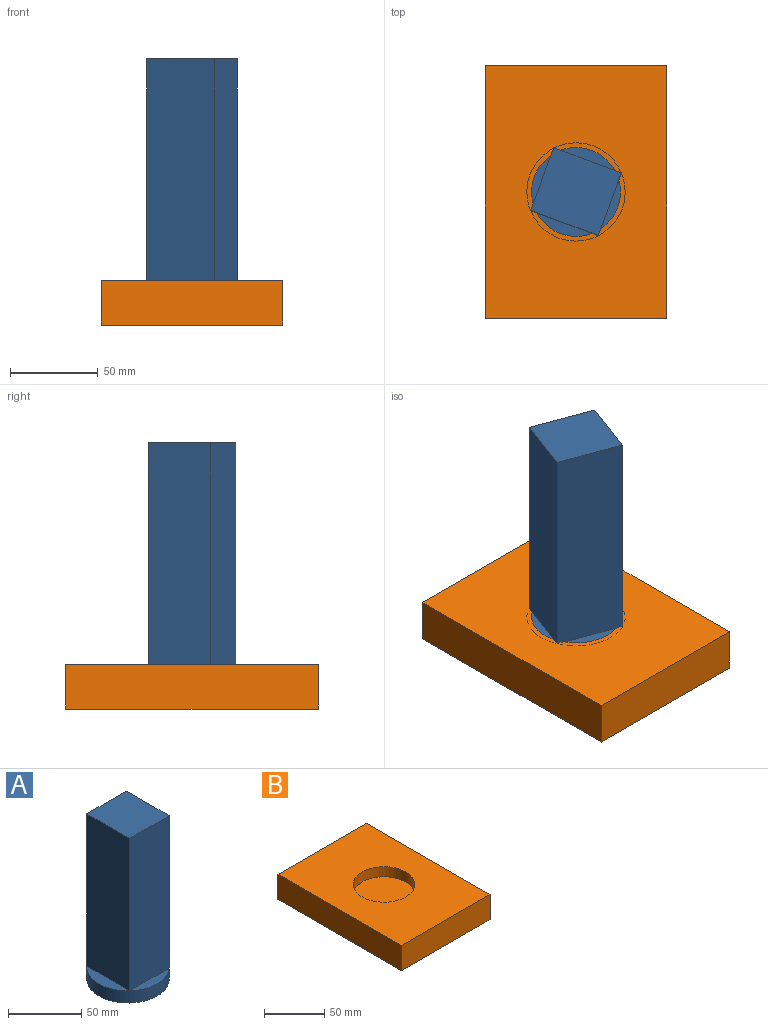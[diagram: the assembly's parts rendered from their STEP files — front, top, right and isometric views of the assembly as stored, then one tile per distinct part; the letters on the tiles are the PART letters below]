
ASSEMBLY  parts=2 mates=1
PART A: 11 faces, bbox 56.2x56.2x137.2 mm
  f0: plane 38.1x7.45mm, normal (0,0,1), area 194.9mm2, adj f3,f6
  f1: plane 41.26x9.03mm, normal (0,0,1), area 257.7mm2, adj f3,f9
  f2: plane 38.1x7.45mm, normal (0,0,1), area 194.9mm2, adj f3,f8
  f3: cylinder r=28.08mm len=56.16mm, axis (0,0,-1), area 1792.6mm2, adj f0,f1,f2,f4,f5
  f4: plane 41.26x9.03mm, normal (0,0,1), area 257.7mm2, adj f3,f7
  f5: plane 56.16x56.16mm, normal (0,0,-1), area 2477.4mm2, adj f3
  f6: plane 127x38.1mm, normal (0,1,0), area 4838.7mm2, adj f0,f7,f9,f10
  f7: plane 127x41.26mm, normal (-1,0,0), area 5240.4mm2, adj f4,f6,f8,f10
  f8: plane 127x38.1mm, normal (0,-1,0), area 4838.7mm2, adj f2,f7,f9,f10
  f9: plane 127x41.26mm, normal (1,0,0), area 5240.4mm2, adj f1,f6,f8,f10
  f10: plane 41.26x38.1mm, normal (0,0,1), area 1572.1mm2, adj f6,f7,f8,f9
PART B: 8 faces, bbox 103.5x144.4x25.4 mm
  f0: plane 103.48x25.4mm, normal (0,1,0), area 2628.4mm2, adj f1,f3,f4,f5
  f1: plane 144.39x25.4mm, normal (-1,0,0), area 3667.5mm2, adj f0,f2,f4,f5
  f2: plane 103.48x25.4mm, normal (0,-1,0), area 2628.4mm2, adj f1,f3,f4,f5
  f3: plane 144.39x25.4mm, normal (1,0,0), area 3667.5mm2, adj f0,f2,f4,f5
  f4: plane 144.39x103.48mm, normal (0,0,1), area 12914.5mm2, adj f0,f1,f2,f3,f6
  f5: plane 144.39x103.48mm, normal (0,0,-1), area 14941.3mm2, adj f0,f1,f2,f3
  f6: cylinder r=25.4mm len=50.8mm, axis (0,0,1), area 1621.5mm2, adj f4,f7
  f7: plane 50.8x50.8mm, normal (0,0,1), area 2026.8mm2, adj f6
PLACE A rot(axis=(0,0,1),69.6deg) t=(0.97,3.75,-0.55)mm
PLACE B t=(0.97,3.75,-15.4)mm fixed
MATE cylindrical B.f6 <-> A.f3  axis (0,0,1) through (0.97,3.75,10)mm
